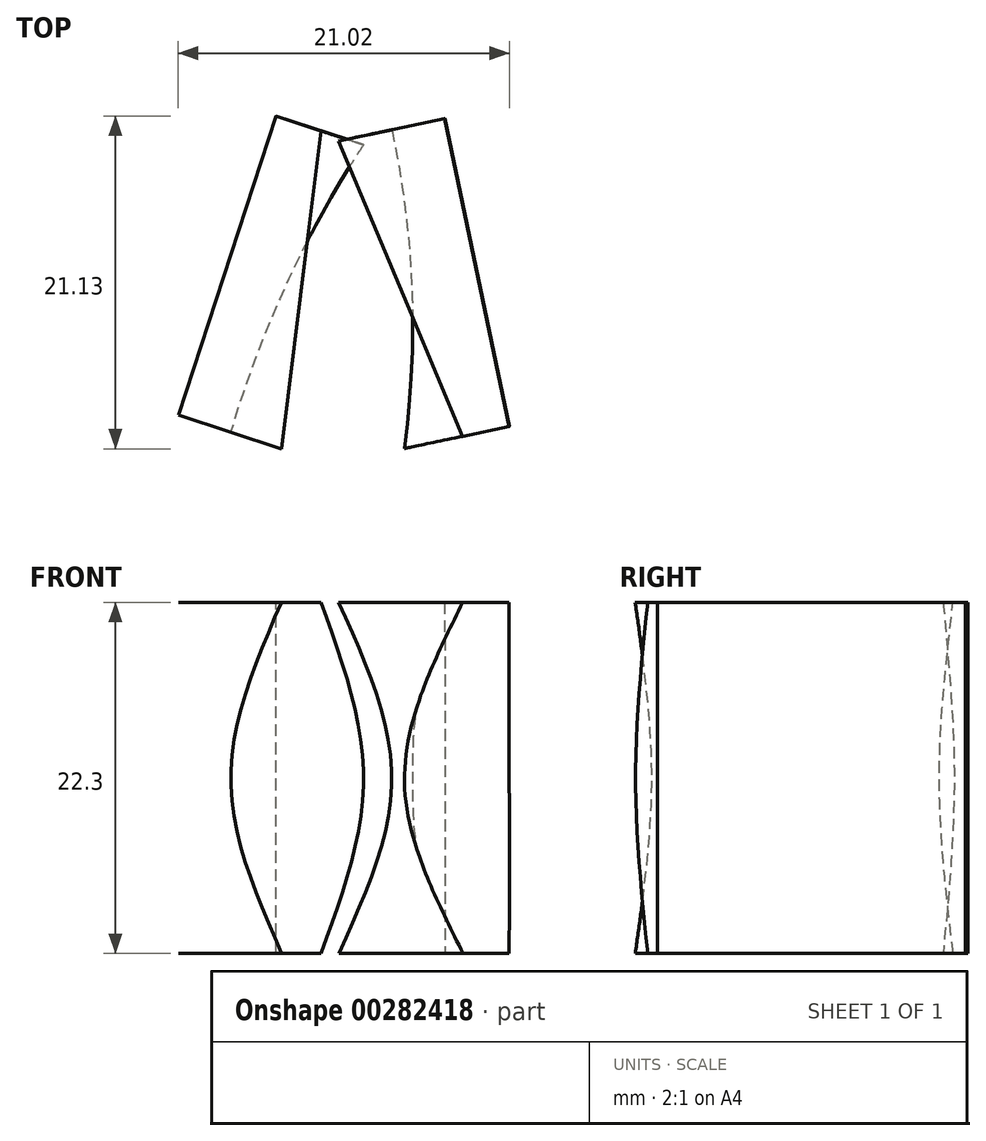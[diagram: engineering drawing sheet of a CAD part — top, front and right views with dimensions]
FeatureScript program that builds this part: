
annotation { "Feature Type Name" : "Feature", "Feature Type Description" : "" }
export const myFeature = defineFeature(function(context is Context, id is Id, definition is map)
    precondition{}
    {
        {
            var Q0;
            Q0=qCreatedBy(makeId("Top.planeOp"),FACE);
            cPlane(context, id + "F0", {"entities" : qUnion([Q0]), "cplaneType" : CPlaneType.OFFSET, "offset" : 11 * mm, "width" : 150 * mm, "height" : 150 * mm});
        }
        {
            var Q0;
            Q0=qCreatedBy(makeId("Top.planeOp"),FACE);
            cPlane(context, id + "F1", {"entities" : qUnion([Q0]), "cplaneType" : CPlaneType.OFFSET, "offset" : 22.3 * mm, "width" : 150 * mm, "height" : 150 * mm});
        }
        {
            var Q0;
            Q0=qCreatedBy(makeId("Top.planeOp"),FACE);
            var sketch = newSketch(context, id + "F2", { "sketchPlane" : qUnion([Q0])});
            skLineSegment(sketch, "E0.bottom", {"start": v(12, -12) * mm, "end": v(-12, -12) * mm, "construction": true});
            skLineSegment(sketch, "E0.top", {"start": v(12, 12) * mm, "end": v(-12, 12) * mm, "construction": true});
            skLineSegment(sketch, "E0.left", {"start": v(12, -12) * mm, "end": v(12, 12) * mm, "construction": true});
            skLineSegment(sketch, "E0.right", {"start": v(-12, -12) * mm, "end": v(-12, 12) * mm, "construction": true});
            skPoint(sketch, "E0.middle", {"position": v(0, 0) * mm});
            skPoint(sketch, "E1.middle", {"position": v(-1.39, -1.74) * mm});
            skLineSegment(sketch, "E2", {"start": v(5.9, 10.79) * mm, "end": v(9.98, -8.77) * mm});
            skLineSegment(sketch, "E3", {"start": v(9.98, -8.77) * mm, "end": v(7.04, -9.38) * mm});
            skLineSegment(sketch, "E4", {"start": v(5.9, 10.79) * mm, "end": v(-0.84, 9.38) * mm});
            skLineSegment(sketch, "E5", {"start": v(7.04, -9.38) * mm, "end": v(-0.84, 9.38) * mm});
            skPoint(sketch, "E6.middle", {"position": v(1.54, -0.8) * mm});
            skLineSegment(sketch, "E7", {"start": v(-11.02, -8.04) * mm, "end": v(-4.82, 10.95) * mm});
            skLineSegment(sketch, "E8", {"start": v(-4.82, 10.95) * mm, "end": v(-1.97, 10.02) * mm});
            skLineSegment(sketch, "E9", {"start": v(-11.02, -8.04) * mm, "end": v(-4.48, -10.18) * mm});
            skLineSegment(sketch, "E10", {"start": v(-1.97, 10.02) * mm, "end": v(-4.48, -10.18) * mm});
            skSolve(sketch);
        }
        {
            var Q0;
            Q0=qCreatedBy(id+"F0.planeOp",FACE);
            var sketch = newSketch(context, id + "F3", { "sketchPlane" : qUnion([Q0])});
            skPoint(sketch, "E11.0", {"position": v(-11.02, -8.04) * mm});
            skLineSegment(sketch, "E12.0", {"start": v(-11.02, -8.04) * mm, "end": v(-4.82, 10.95) * mm});
            skLineSegment(sketch, "E13", {"start": v(-11.02, -8.04) * mm, "end": v(-7.71, -9.12) * mm});
            skLineSegment(sketch, "E14", {"start": v(-4.82, 10.95) * mm, "end": v(0.95, 9.06) * mm});
            skArc(sketch, "E15", {"start": v(0.95, 9.48) * mm, "mid": v(-4.07, 0.5) * mm, "end": v(-7.71, -9.12) * mm});
            skPoint(sketch, "E16.0", {"position": v(9.98, -8.77) * mm});
            skLineSegment(sketch, "E17.0", {"start": v(5.9, 10.79) * mm, "end": v(9.98, -8.77) * mm});
            skLineSegment(sketch, "E18", {"start": v(9.98, -8.77) * mm, "end": v(3.32, -10.16) * mm});
            skLineSegment(sketch, "E19", {"start": v(5.9, 10.79) * mm, "end": v(2.52, 10.08) * mm});
            skArc(sketch, "E20", {"start": v(3.32, -10.16) * mm, "mid": v(3.8, 0) * mm, "end": v(2.52, 10.08) * mm});
            skSolve(sketch);
        }
        {
            var Q0;
            Q0=qCreatedBy(id+"F1.planeOp",FACE);
            var sketch = newSketch(context, id + "F4", { "sketchPlane" : qUnion([Q0])});
            skLineSegment(sketch, "E21.bottom", {"start": v(11.98, -12) * mm, "end": v(-12.02, -12) * mm, "construction": true});
            skLineSegment(sketch, "E21.top", {"start": v(11.98, 12) * mm, "end": v(-12.02, 12) * mm, "construction": true});
            skLineSegment(sketch, "E21.left", {"start": v(11.98, -12) * mm, "end": v(11.98, 12) * mm, "construction": true});
            skLineSegment(sketch, "E21.right", {"start": v(-12.02, -12) * mm, "end": v(-12.02, 12) * mm, "construction": true});
            skPoint(sketch, "E21.middle", {"position": v(-0.02, 0) * mm});
            skPoint(sketch, "E22.middle", {"position": v(-1.4, -1.74) * mm});
            skLineSegment(sketch, "E23", {"start": v(5.88, 10.78) * mm, "end": v(9.96, -8.77) * mm});
            skLineSegment(sketch, "E24", {"start": v(9.96, -8.77) * mm, "end": v(7.03, -9.39) * mm});
            skLineSegment(sketch, "E25", {"start": v(5.88, 10.78) * mm, "end": v(-0.85, 9.38) * mm});
            skLineSegment(sketch, "E26", {"start": v(7.03, -9.39) * mm, "end": v(-0.85, 9.38) * mm});
            skPoint(sketch, "E27.middle", {"position": v(1.52, -0.81) * mm});
            skLineSegment(sketch, "E28", {"start": v(-11.04, -8.05) * mm, "end": v(-4.84, 10.94) * mm});
            skLineSegment(sketch, "E29", {"start": v(-4.84, 10.94) * mm, "end": v(-1.99, 10.01) * mm});
            skLineSegment(sketch, "E30", {"start": v(-11.04, -8.05) * mm, "end": v(-4.5, -10.18) * mm});
            skLineSegment(sketch, "E31", {"start": v(-1.99, 10.01) * mm, "end": v(-4.5, -10.18) * mm});
            skSolve(sketch);
        }
        {
            var Q0;
            Q0=makeQuery(id+"F2.imprint","IMPRINT",FACE,{"disambiguationData":[TD([[makeQuery(id+"F2.imprint","IMPRINT",EDGE,{"derivedFrom":sQuery(id+"F2.wireOp",EDGE,"E7")}),-1.0]])]});
            var Q1;
            {var subQ0=sQuery(id+"F3.wireOp",EDGE,"E12.0");Q1=makeQuery(id+"F3.imprint","IMPRINT",FACE,{"disambiguationData":[TD([[makeQuery(id+"F3.imprint","IMPRINT",EDGE,{"derivedFrom":subQ0}),-1.0]])]});}
            var Q2;
            Q2=makeQuery(id+"F4.imprint","IMPRINT",FACE,{"disambiguationData":[TD([[makeQuery(id+"F4.imprint","IMPRINT",EDGE,{"derivedFrom":sQuery(id+"F4.wireOp",EDGE,"E28")}),-1.0]])]});
            loft(context, id + "F5", {"sheetProfilesArray" : [{ "sheetProfileEntities" : qUnion([Q0]) }, { "sheetProfileEntities" : qUnion([Q1]) }, { "sheetProfileEntities" : qUnion([Q2]) }]});
        }
        {
            var Q0;
            Q0=makeQuery(id+"F4.imprint","IMPRINT",FACE,{"disambiguationData":[TD([[makeQuery(id+"F4.imprint","IMPRINT",EDGE,{"derivedFrom":sQuery(id+"F4.wireOp",EDGE,"E23")}),-1.0]])]});
            var Q1;
            Q1=makeQuery(id+"F3.imprint","IMPRINT",FACE,{"disambiguationData":[TD([[makeQuery(id+"F3.imprint","IMPRINT",EDGE,{"derivedFrom":sQuery(id+"F3.wireOp",EDGE,"E17.0")}),-1.0]])]});
            var Q2;
            Q2=makeQuery(id+"F2.imprint","IMPRINT",FACE,{"disambiguationData":[TD([[makeQuery(id+"F2.imprint","IMPRINT",EDGE,{"derivedFrom":sQuery(id+"F2.wireOp",EDGE,"E2")}),-1.0]])]});
            loft(context, id + "F6", {"sheetProfilesArray" : [{ "sheetProfileEntities" : qUnion([Q0]) }, { "sheetProfileEntities" : qUnion([Q1]) }, { "sheetProfileEntities" : qUnion([Q2]) }]});
        }
    });
